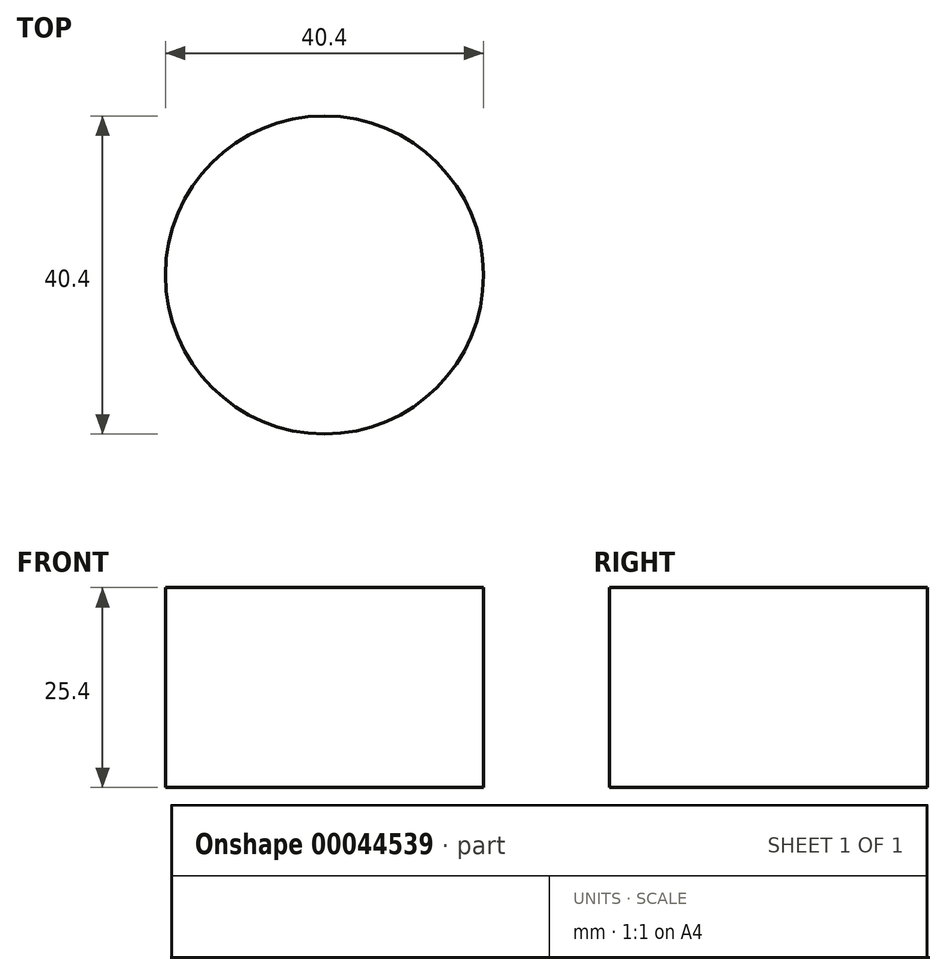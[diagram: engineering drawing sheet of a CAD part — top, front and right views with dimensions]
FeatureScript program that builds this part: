
annotation { "Feature Type Name" : "Feature", "Feature Type Description" : "" }
export const myFeature = defineFeature(function(context is Context, id is Id, definition is map)
    precondition{}
    {
        {
            var Q0;
            Q0=qCreatedBy(makeId("Top.planeOp"),FACE);
            var sketch = newSketch(context, id + "F0", { "sketchPlane" : qUnion([Q0])});
            skCircle(sketch, "E0", {"center": v(0, 0) * mm, "radius": 20.2 * mm});
            skSolve(sketch);
        }
        {
            var Q0;
            Q0 = qSketchRegion(id + "F0", true);
            extrude(context, id + "F1", {"entities" : qUnion([Q0]), "depth" : 25.4 * mm});
        }
    });
